# Revit family: Storage-Mounted-Teknion-BOCSG_Overhead_Cabinet_Glass_Overlay_Sliding_Door-R2019
name_source: partatom
category: Casework
units: mm (PartAtom-declared; Revit-internal decimal feet)

## family parameters
Always vertical = Yes
Cut with Voids When Loaded = No
OmniClass Number = 23.40.20.00
OmniClass Title = General Furniture and Specialties
Room Calculation Point = No
Shared = Yes
Work Plane-Based = No

## types (2) — shared parameters
Assembly Code = E2020200
Manufacturer = Teknion
Manufacturer Fax = 416.661.4586
Part Number = BOCSG
Product Documentation Link = https://www.teknion.com
Product Line = Expansion Casegoods
Product Page URL = https://www.teknion.com
Series = Expansion Casegoods
Sustainability Data = https://www.teknion.com
URL = www.teknion.com
Unit Weight URL = http://www.teknion.com
Warranty = http://www.teknion.com

## per-type parameters (varying)
| type | Depth | Description | Model |
| Wall-Panel Mounted, One Door Configuration, 18" Depth | 18 " | Overhead Cabinet – Glass Overlay Sliding Door, Wall-Panel Mounted, One Door, 18" Depth, 15" Height | BOCSGBO18__15_ |
| Wall-Mounted, One Door Configuration, 16" Depth | 16.673 " | Overhead Cabinet – Glass Overlay Sliding Door, Wall-Mounted, One Door, 16" Depth, 15" Height | BOCSGWO16__15_ |

## geometry (parser evidence)
native form markers: Sweep x2
no freeform markers — native parametric forms only
